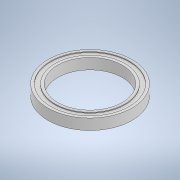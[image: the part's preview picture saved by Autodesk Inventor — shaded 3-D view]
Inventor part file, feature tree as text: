
AUTODESK INVENTOR PART (.ipt)
format: ipt  version: 2020 (Build 240168000, 168)  size: 134,144 bytes
history: native  units: mm
features: extrude x3, sketch x3
ambient origin geometry x8: Origin, YZ Plane, XZ Plane, XY Plane, X Axis, Y Axis, Z Axis, Center Point
bodies: Solid1 (feature_tree)
feature tree (6):
  extrude  "Extrusion1"  Depth=78.0mm
  extrude  "Extrusion2"  Depth=10.0mm
  extrude  "Extrusion3"  Depth=0.7mm TaperAngle=0.0deg
  sketch  "Sketch1"  dims[d0=60.0mm d1=78.0mm]
  sketch  "Sketch2"  dims[d2=10.0mm d3=0.0mm d4=65.0mm]
  sketch  "Sketch3"  dims[d5=73.0mm d6=0.7mm d7=0.0mm d8=0.7mm d9=0.0mm]
